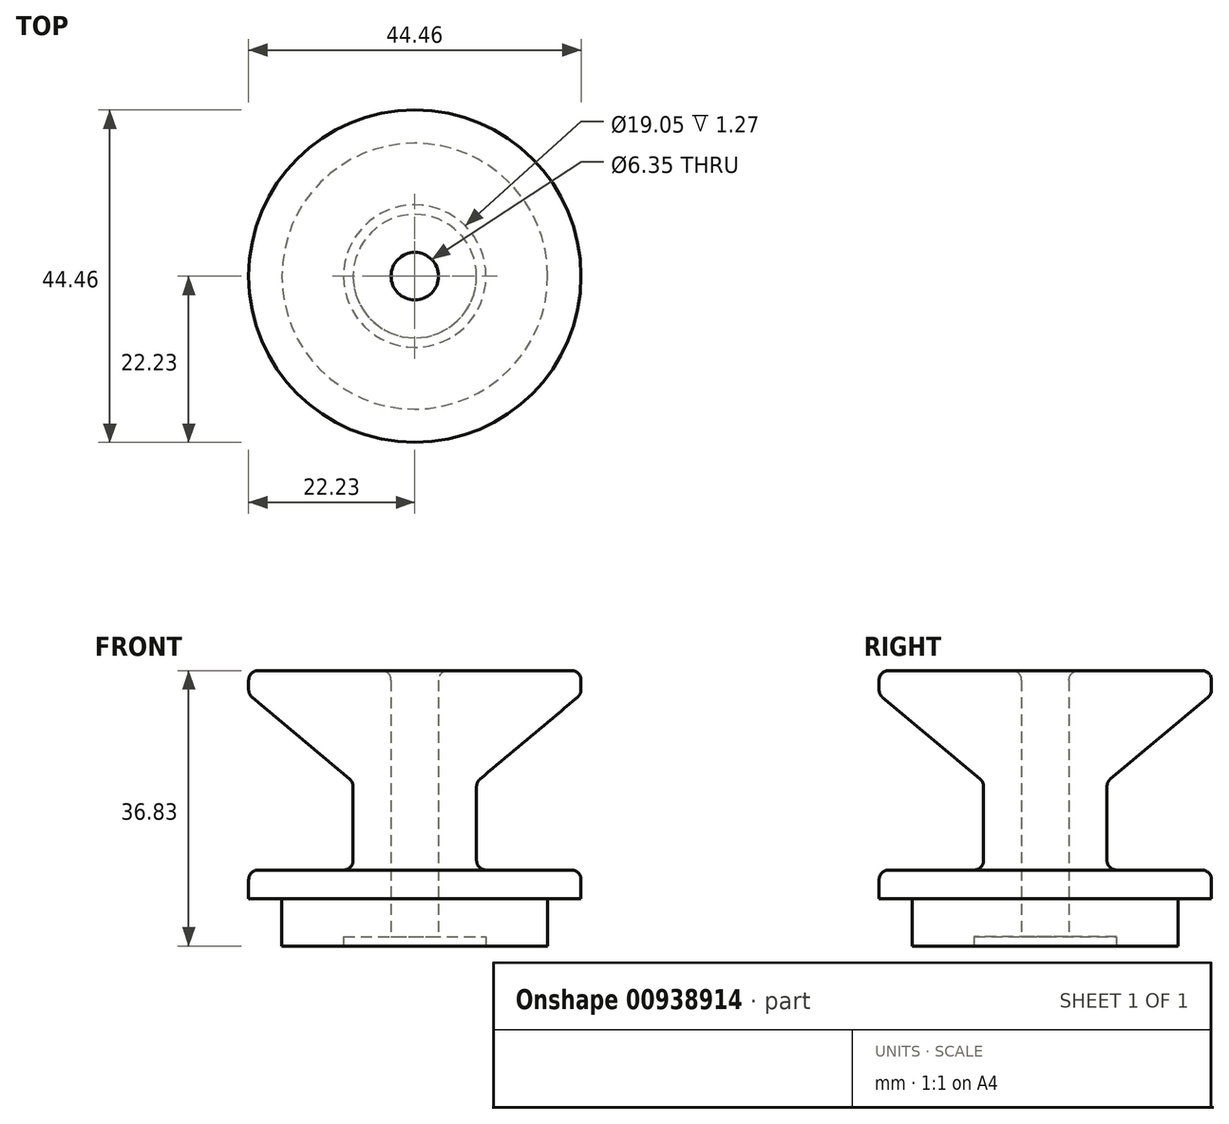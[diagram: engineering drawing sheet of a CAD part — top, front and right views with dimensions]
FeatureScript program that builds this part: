
annotation { "Feature Type Name" : "Feature", "Feature Type Description" : "" }
export const myFeature = defineFeature(function(context is Context, id is Id, definition is map)
    precondition{}
    {
        {
            var Q0;
            Q0=qCreatedBy(makeId("Front.planeOp"),FACE);
            var sketch = newSketch(context, id + "F0", { "sketchPlane" : qUnion([Q0])});
            skLineSegment(sketch, "E0", {"start": v(0, 0) * mm, "end": v(0, 36.83) * mm, "construction": true});
            skLineSegment(sketch, "E1", {"start": v(-3.17, 1.27) * mm, "end": v(-9.52, 1.27) * mm});
            skLineSegment(sketch, "E2", {"start": v(-9.52, 1.27) * mm, "end": v(-9.52, 0) * mm});
            skLineSegment(sketch, "E3", {"start": v(-9.53, 0) * mm, "end": v(-17.78, 0) * mm});
            skLineSegment(sketch, "E4", {"start": v(-22.23, 6.35) * mm, "end": v(-22.23, 10.16) * mm});
            skLineSegment(sketch, "E5", {"start": v(-22.23, 10.16) * mm, "end": v(-8.25, 10.16) * mm});
            skLineSegment(sketch, "E6", {"start": v(-8.26, 10.16) * mm, "end": v(-8.26, 21.93) * mm});
            skLineSegment(sketch, "E7", {"start": v(-8.26, 21.93) * mm, "end": v(-22.22, 33.66) * mm});
            skLineSegment(sketch, "E8", {"start": v(-22.23, 33.66) * mm, "end": v(-22.23, 36.83) * mm});
            skLineSegment(sketch, "E9", {"start": v(-22.23, 36.83) * mm, "end": v(-3.18, 36.83) * mm});
            skLineSegment(sketch, "E10", {"start": v(-3.18, 36.83) * mm, "end": v(-3.18, 1.27) * mm});
            skLineSegment(sketch, "E11", {"start": v(-22.23, 33.66) * mm, "end": v(-22.22, 10.16) * mm, "construction": true});
            skLineSegment(sketch, "E12", {"start": v(-22.23, 6.35) * mm, "end": v(-17.78, 6.35) * mm});
            skLineSegment(sketch, "E13", {"start": v(-17.78, 6.35) * mm, "end": v(-17.78, 0) * mm});
            skSolve(sketch);
        }
        {
            var Q0;
            Q0 = qSketchRegion(id + "F0", true);
            var Q1;
            Q1=sQuery(id+"F0.wireOp",EDGE,"E0");
            revolve(context, id + "F1", {"surfaceOperationType" : NewSurfaceOperationType.NEW, "entities" : qUnion([Q0]), "axis" : qUnion([Q1]), "revolveType" : RevolveType.FULL});
        }
        {
            var Q0;
            Q0=makeQuery(id+"F1.opRevolve","SWEPT_EDGE",EDGE,{"disambiguationData":[OSD([sQuery(id+"F0.wireOp",EDGE,"E8"),sQuery(id+"F0.wireOp",EDGE,"E9")])]});
            var Q1;
            Q1=makeQuery(id+"F1.opRevolve","SWEPT_EDGE",EDGE,{"disambiguationData":[OSD([sQuery(id+"F0.wireOp",EDGE,"E7"),sQuery(id+"F0.wireOp",EDGE,"E8")])]});
            var Q2;
            Q2=makeQuery(id+"F1.opRevolve","SWEPT_EDGE",EDGE,{"disambiguationData":[OSD([sQuery(id+"F0.wireOp",EDGE,"E6"),sQuery(id+"F0.wireOp",EDGE,"E7")])]});
            var Q3;
            Q3=makeQuery(id+"F1.opRevolve","SWEPT_EDGE",EDGE,{"disambiguationData":[OSD([sQuery(id+"F0.wireOp",EDGE,"E5"),sQuery(id+"F0.wireOp",EDGE,"E6")])]});
            var Q4;
            Q4=makeQuery(id+"F1.opRevolve","SWEPT_EDGE",EDGE,{"disambiguationData":[OSD([sQuery(id+"F0.wireOp",EDGE,"E4"),sQuery(id+"F0.wireOp",EDGE,"E5")])]});
            var Q5;
            Q5=makeQuery(id+"F1.opRevolve","SWEPT_EDGE",EDGE,{"disambiguationData":[OSD([sQuery(id+"F0.wireOp",EDGE,"E9"),sQuery(id+"F0.wireOp",EDGE,"E10")])]});
            fillet(context, id + "F2", {"entities" : qUnion([Q0, Q1, Q2, Q3, Q4, Q5]), "radius" : 1.27 * mm, "tangentPropagation" : true, "allowEdgeOverflow" : false});
        }
    });
